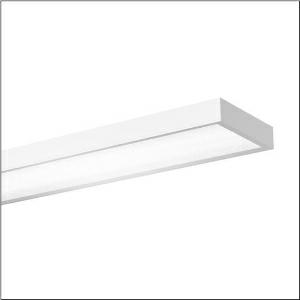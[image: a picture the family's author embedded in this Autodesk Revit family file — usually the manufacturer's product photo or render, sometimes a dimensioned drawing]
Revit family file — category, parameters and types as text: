
# Revit family: sport_31_51hs12dd4gca
name_source: partatom
category: Lighting Fixtures
units: mm (PartAtom-declared; Revit-internal decimal feet)

## family parameters
Cut with Voids When Loaded = No
Host = Face
Light Source = No
Part Type = Normal
Room Calculation Point = No
Round Connector Dimension = Use Diameter
Shared = No

## types (1)
- --- (1 x LED, 15290 lm, 113 W, 4000K)
    Apparent Load = 113 VA
    CIE Flux Codes = 65 89 97 100 100
    Color Rendering = 80
    Color Temperature = 4000K
    Default Elevation = 1800 mm
    Description = Sport 31, LED high bay luminaire, primary light control with reflector, of sheet steel, primary anti-glare with prismatic structure, of PC, primary optical cover: cover panel, of PC, light emission: direct distribution, primary light characteristic: symmetric, installation type: suspended mounting, recessed, surface-mounted, LED, rated luminous flux: 16.000lm, luminous efficacy: 137lm/W, light colour: 840, colour temperature: 4000K, control gear: DALI 2, with terminal, 5-pole, max. 2.5mm², mains connection: 220..240V, AC/DC, 50/60Hz, rated input power: 117W, housing, of sheet steel, traffic white (RAL 9016), length: 1.540mm, width: 415mm, height: 95mm, protection rating (complete): IP20, protection rating (lamp compartment, on room side): IP50, insulation class (complete): insulation class I (protective earthing), certification: CE, ENEC, UKCA, ball protection: ball impact resistant with ceiling mounting or chain suspension, impact resistance: IK08, permissible operating ambient temperature: -20..+35°C, standard: DIN 18032-3, EN 60598-2-22, packaging unit: 1 piece
    Height = 100 mm  [stored 0.328084 ft]
    Lamp = 1 x LED
    Lamp Light Flux = 15290 lm
    Lamp Power = 113 W
    Lamp count = 1
    Length = 1500 mm
    Luminous efficacy = 135 lm/W
    Manufacturer = Siteco
    ModVariant = No
    Model = 51HS12DD4GCA
    Mounting Place = Ceiling
    Mounting Type = Pendant
    Number of Poles = 1
    OnlyDefault = Yes
    Power Factor = 1
    Product Name = Sport 31
    Product group = LED high bay luminaire
    ProductGroupID = 903
    Protection Class = Protection class I
    Protection Degree = IP 20
    RLX_Detail_Level = 1
    RLX_Emergency_Light_Flux = 0 lm
    RLX_Emergency_Type = 0
    RLX_Emergency_Type_DB = No
    RlxData = <blob elided: 24061 chars, md5=1698a779>
    Socket = socket
    Standby Power = 0 W
    System Light Flux = 15290 lm
    System Power = 113 W
    Type Comments = factory setting: luminous flux: 100 % | dim-lin: 254 | 558 mA
    Type Image = l_1006829.jpg
    URL = http://relux.com
    VarID = @adj_197138
    Voltage = 0 V
    Weight = 0.00 kg
    Width = 415 mm

note: [stored X ft] marks values corroborated as IEEE doubles in the binary element streams (Revit-internal decimal feet)

## geometry (parser evidence)
native form markers: Blend x4, Sweep x11
no freeform markers — native parametric forms only
